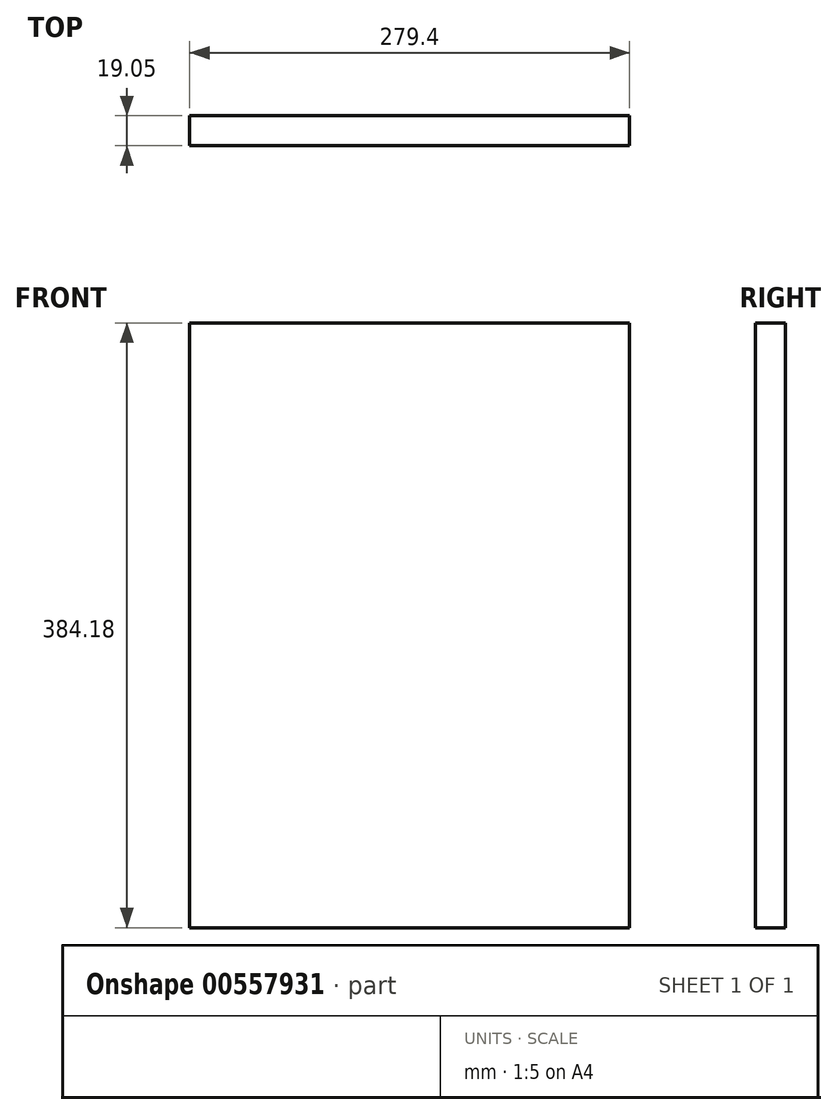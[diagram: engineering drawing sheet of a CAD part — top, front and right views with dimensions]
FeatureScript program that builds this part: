
annotation { "Feature Type Name" : "Feature", "Feature Type Description" : "" }
export const myFeature = defineFeature(function(context is Context, id is Id, definition is map)
    precondition{}
    {
        {
            var Q0;
            Q0=qCreatedBy(makeId("Front.planeOp"),FACE);
            var sketch = newSketch(context, id + "F0", { "sketchPlane" : qUnion([Q0])});
            skLineSegment(sketch, "E0.bottom", {"start": v(302.26, 20.32) * mm, "end": v(22.86, 20.32) * mm});
            skLineSegment(sketch, "E0.top", {"start": v(302.26, 404.5) * mm, "end": v(22.86, 404.5) * mm});
            skLineSegment(sketch, "E0.left", {"start": v(302.26, 20.32) * mm, "end": v(302.26, 404.5) * mm});
            skLineSegment(sketch, "E0.right", {"start": v(22.86, 20.32) * mm, "end": v(22.86, 404.5) * mm});
            skPoint(sketch, "E0.middle", {"position": v(162.56, 212.4) * mm});
            skSolve(sketch);
        }
        {
            var Q0;
            Q0=makeQuery(id+"F0.imprint","IMPRINT",FACE,{"disambiguationData":[TD([[makeQuery(id+"F0.imprint","IMPRINT",EDGE,{"derivedFrom":sQuery(id+"F0.wireOp",EDGE,"E0.bottom")}),-1.0]])]});
            extrude(context, id + "F1", {"entities" : qUnion([Q0]), "depth" : 19.05 * mm, "offsetDistance" : 25.4 * mm});
        }
    });
